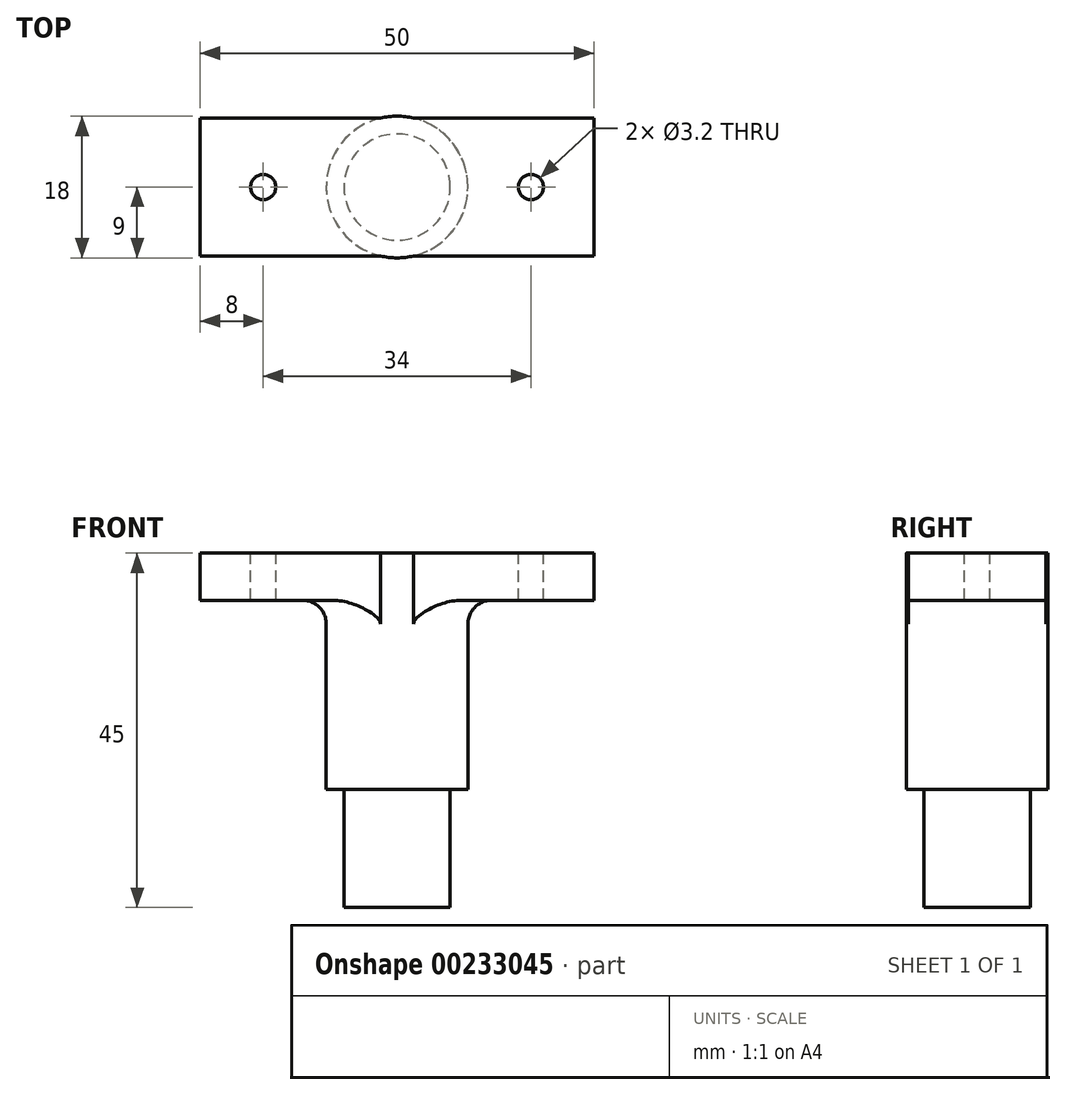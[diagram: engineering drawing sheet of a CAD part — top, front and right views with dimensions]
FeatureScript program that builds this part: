
annotation { "Feature Type Name" : "Feature", "Feature Type Description" : "" }
export const myFeature = defineFeature(function(context is Context, id is Id, definition is map)
    precondition{}
    {
        {
            var Q0;
            Q0=qCreatedBy(makeId("Top.planeOp"),FACE);
            cPlane(context, id + "F0", {"entities" : qUnion([Q0]), "cplaneType" : CPlaneType.OFFSET, "offset" : 40 * mm, "width" : 150 * mm, "height" : 150 * mm});
        }
        {
            var Q0;
            Q0=qCreatedBy(id+"F0.planeOp",FACE);
            var sketch = newSketch(context, id + "F1", { "sketchPlane" : qUnion([Q0])});
            skCircle(sketch, "E0", {"center": v(0, 0) * mm, "radius": 6.75 * mm});
            skSolve(sketch);
        }
        {
            var Q0;
            Q0=makeQuery(id+"F1.imprint","IMPRINT",FACE,{"disambiguationData":[TD([[makeQuery(id+"F1.imprint","IMPRINT",EDGE,{"derivedFrom":sQuery(id+"F1.wireOp",EDGE,"E0")}),1.0]])]});
            extrude(context, id + "F2", {"entities" : qUnion([Q0]), "oppositeDirection" : true, "depth" : 15 * mm});
        }
        {
            var Q0;
            Q0=qCreatedBy(id+"F0.planeOp",FACE);
            var sketch = newSketch(context, id + "F3", { "sketchPlane" : qUnion([Q0])});
            skCircle(sketch, "E1", {"center": v(0, 0) * mm, "radius": 9 * mm});
            skSolve(sketch);
        }
        {
            var Q0;
            Q0=makeQuery(id+"F3.imprint","IMPRINT",FACE,{"disambiguationData":[TD([[makeQuery(id+"F3.imprint","IMPRINT",EDGE,{"derivedFrom":sQuery(id+"F3.wireOp",EDGE,"E1")}),1.0]])]});
            extrude(context, id + "F4", {"entities" : qUnion([Q0]), "operationType" : NewBodyOperationType.ADD, "depth" : 30 * mm});
        }
        {
            var Q0;
            Q0=makeQuery(id+"F4.opExtrude","CAP_FACE",FACE,{"disambiguationData":[OSD([sQuery(id+"F3.wireOp",EDGE,"E1")])],"isStart":false});
            var sketch = newSketch(context, id + "F5", { "sketchPlane" : qUnion([Q0])});
            skLineSegment(sketch, "E2.bottom", {"start": v(-25, 8.75) * mm, "end": v(25, 8.75) * mm});
            skLineSegment(sketch, "E2.top", {"start": v(-25, -8.75) * mm, "end": v(25, -8.75) * mm});
            skLineSegment(sketch, "E2.left", {"start": v(-25, 8.75) * mm, "end": v(-25, -8.75) * mm});
            skLineSegment(sketch, "E2.right", {"start": v(25, 8.75) * mm, "end": v(25, -8.75) * mm});
            skCircle(sketch, "E3", {"center": v(-17, 0) * mm, "radius": 1.6 * mm});
            skCircle(sketch, "E4", {"center": v(17, 0) * mm, "radius": 1.6 * mm});
            skSolve(sketch);
        }
        {
            var Q0;
            {var subQ0=sQuery(id+"F5.wireOp",EDGE,"E2.left");Q0=makeQuery(id+"F5.imprint","IMPRINT",FACE,{"disambiguationData":[TD([[makeQuery(id+"F5.imprint","IMPRINT",EDGE,{"derivedFrom":subQ0}),1.0]])]});}
            var Q1;
            {var subQ0=sQuery(id+"F5.wireOp",EDGE,"E2.right");Q1=makeQuery(id+"F5.imprint","IMPRINT",FACE,{"disambiguationData":[TD([[makeQuery(id+"F5.imprint","IMPRINT",EDGE,{"derivedFrom":subQ0}),-1.0]])]});}
            var Q2;
            {var subQ0=sQuery(id+"F5.wireOp",EDGE,"E2.bottom");var subQ1=makeQuery(id+"F4.opExtrude","CAP_EDGE",EDGE,{"disambiguationData":[OSD([sQuery(id+"F3.wireOp",EDGE,"E1")])],"isStart":false});var subQ2=makeQuery(id+"F5.imprint","INTERSECT",VERTEX,{"disambiguationData":[OD(0.0)],"derivedFrom":[subQ1,subQ0]});Q2=makeQuery(id+"F5.imprint","IMPRINT",FACE,{"disambiguationData":[TD([[makeQuery(id+"F5.imprint","IMPRINT",EDGE,{"disambiguationData":[TD([[subQ2,-1.0]])],"derivedFrom":subQ0}),-1.0]])]});}
            var Q3;
            {var subQ0=sQuery(id+"F5.wireOp",EDGE,"E2.top");var subQ1=makeQuery(id+"F4.opExtrude","CAP_EDGE",EDGE,{"disambiguationData":[OSD([sQuery(id+"F3.wireOp",EDGE,"E1")])],"isStart":false});var subQ2=makeQuery(id+"F5.imprint","INTERSECT",VERTEX,{"disambiguationData":[OD(0.0)],"derivedFrom":[subQ1,subQ0]});Q3=makeQuery(id+"F5.imprint","IMPRINT",FACE,{"disambiguationData":[TD([[makeQuery(id+"F5.imprint","IMPRINT",EDGE,{"disambiguationData":[TD([[subQ2,-1.0]])],"derivedFrom":subQ0}),-1.0]])]});}
            var Q4;
            {var subQ0=sQuery(id+"F5.wireOp",EDGE,"E2.bottom");var subQ1=makeQuery(id+"F4.opExtrude","CAP_EDGE",EDGE,{"disambiguationData":[OSD([sQuery(id+"F3.wireOp",EDGE,"E1")])],"isStart":false});var subQ2=makeQuery(id+"F5.imprint","INTERSECT",VERTEX,{"disambiguationData":[OD(0.0)],"derivedFrom":[subQ1,subQ0]});Q4=makeQuery(id+"F5.imprint","IMPRINT",FACE,{"disambiguationData":[TD([[makeQuery(id+"F5.imprint","IMPRINT",EDGE,{"disambiguationData":[TD([[subQ2,-1.0]])],"derivedFrom":subQ0}),1.0]])]});}
            extrude(context, id + "F6", {"entities" : qUnion([Q0, Q1, Q2, Q3, Q4]), "operationType" : NewBodyOperationType.ADD, "oppositeDirection" : true, "depth" : 6 * mm});
        }
        {
            var Q0;
            {var subQ0=sQuery(id+"F3.wireOp",EDGE,"E1");Q0=makeQuery(id+"F6.boolean.opBoolean","INTERSECT",EDGE,{"disambiguationData":[OD(0.0)],"derivedFrom":[makeQuery(id+"F4.opExtrude","SWEPT_FACE",FACE,{"disambiguationData":[OSD([subQ0])]}),makeQuery(id+"F6.opExtrude","CAP_FACE",FACE,{"disambiguationData":[OSD([subQ0,sQuery(id+"F5.wireOp",EDGE,"E2.bottom"),sQuery(id+"F5.wireOp",EDGE,"E2.top"),sQuery(id+"F5.wireOp",EDGE,"E2.left"),sQuery(id+"F5.wireOp",EDGE,"E2.right"),sQuery(id+"F5.wireOp",EDGE,"E3"),sQuery(id+"F5.wireOp",EDGE,"E4")])],"isStart":false})]});}
            var Q1;
            {var subQ0=sQuery(id+"F3.wireOp",EDGE,"E1");Q1=makeQuery(id+"F6.boolean.opBoolean","INTERSECT",EDGE,{"disambiguationData":[OD(1.0)],"derivedFrom":[makeQuery(id+"F4.opExtrude","SWEPT_FACE",FACE,{"disambiguationData":[OSD([subQ0])]}),makeQuery(id+"F6.opExtrude","CAP_FACE",FACE,{"disambiguationData":[OSD([subQ0,sQuery(id+"F5.wireOp",EDGE,"E2.bottom"),sQuery(id+"F5.wireOp",EDGE,"E2.top"),sQuery(id+"F5.wireOp",EDGE,"E2.left"),sQuery(id+"F5.wireOp",EDGE,"E2.right"),sQuery(id+"F5.wireOp",EDGE,"E3"),sQuery(id+"F5.wireOp",EDGE,"E4")])],"isStart":false})]});}
            fillet(context, id + "F7", {"entities" : qUnion([Q0, Q1]), "radius" : 3 * mm, "tangentPropagation" : true, "allowEdgeOverflow" : false});
        }
    });
